# Revit family: G220760JX-001_JUDFP242HX
name_source: partatom
category: Specialty Equipment
units: mm (PartAtom-declared; Revit-internal decimal feet)

## family parameters
Always vertical = Yes
Cut with Voids When Loaded = No
Enable Cutting in Views = No
Maintain Annotation Orientation = No
Part Type = Normal
Room Calculation Point = No
Round Connector Dimension = Use Diameter
Shared = No
Work Plane-Based = No

## types (1)
- JUDFP242HX
    Amps = 0 A
    Back Panel Material = ARCAT - Metal - Aluminum
    Body Material = ARCAT - Metal - Steel - Stainless
    Clearance Material = ARCAT - Clearance
    Default Elevation = 0 "
    Depth = 23.9 "
    Description = Panel-Ready 24" Double-Refrigerator Drawers
Tiroir-réfrigérateur double prêt pour le panneau, 24 po
    Dimension Guide = https://www.whirlpool.com
    Door Material = ARCAT - Metal - Steel - Stainless Door
    Energy Guide = https://www.whirlpool.com
    Family Name = Drawer Specialty
    Feature 1 = Emotive Controls
    Feature 2 = Daring Obsidian Interior
    Feature 3 = Stealth Flush Design
    Handle Material = ARCAT - Metal - Steel -Gray
    Height = 0 "
    Hinge Material = ARCAT - Plastic - Black
    Leg Material = ARCAT - Plastic - Black
    Screw Material = ARCAT - Metal - Steel - Stainless
    Voltage = 0 V
    Width = 23.9 "

## geometry (parser evidence)
native form markers: Sweep x2
no freeform markers — native parametric forms only
